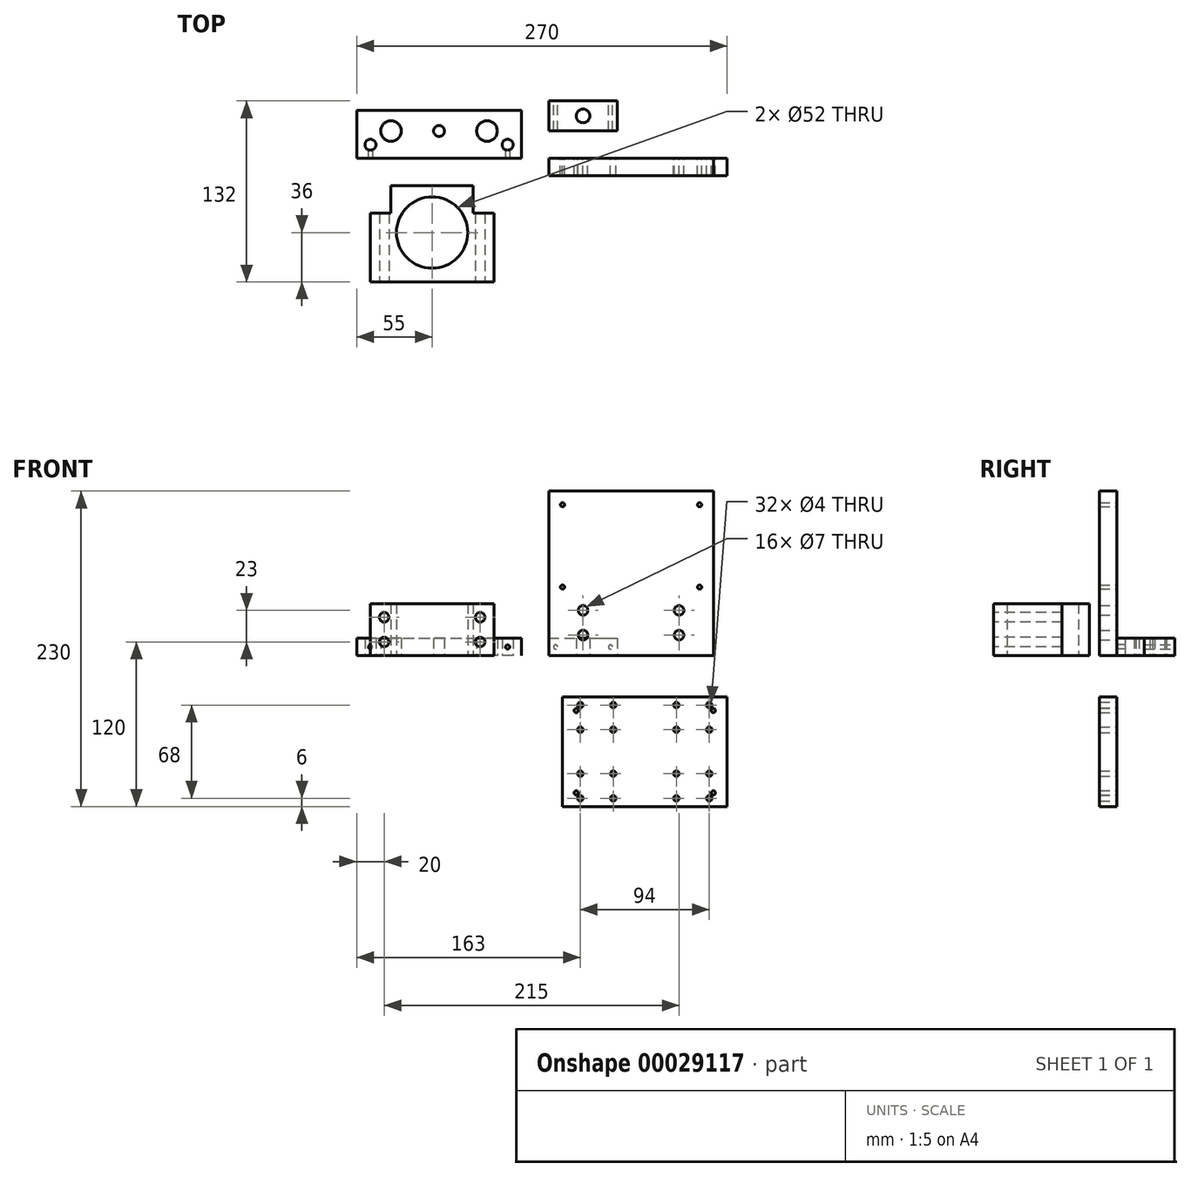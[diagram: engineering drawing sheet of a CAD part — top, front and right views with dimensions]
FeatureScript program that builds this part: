
annotation { "Feature Type Name" : "Feature", "Feature Type Description" : "" }
export const myFeature = defineFeature(function(context is Context, id is Id, definition is map)
    precondition{}
    {
        {
            var Q0;
            Q0=qCreatedBy(makeId("Top.planeOp"),FACE);
            var sketch = newSketch(context, id + "F0", { "sketchPlane" : qUnion([Q0])});
            skLineSegment(sketch, "E0.bottom", {"start": v(-120, 35) * mm, "end": v(0, 35) * mm});
            skLineSegment(sketch, "E0.top", {"start": v(-120, 0) * mm, "end": v(0, 0) * mm});
            skLineSegment(sketch, "E0.left", {"start": v(-120, 35) * mm, "end": v(-120, 0) * mm});
            skLineSegment(sketch, "E0.right", {"start": v(0, 35) * mm, "end": v(0, 0) * mm});
            skCircle(sketch, "E1", {"center": v(-95, 20) * mm, "radius": 7.5 * mm});
            skCircle(sketch, "E2", {"center": v(-60, 20) * mm, "radius": 4 * mm});
            skCircle(sketch, "E3", {"center": v(-25, 20) * mm, "radius": 7.5 * mm});
            skCircle(sketch, "E4", {"center": v(-110, 10) * mm, "radius": 4 * mm});
            skCircle(sketch, "E5", {"center": v(-10, 10) * mm, "radius": 4 * mm});
            skSolve(sketch);
        }
        {
            var Q0;
            Q0 = qSketchRegion(id + "F0", true);
            extrude(context, id + "F1", {"entities" : qUnion([Q0]), "depth" : 12.7 * mm});
        }
        {
            var Q0;
            Q0=makeQuery(id+"F1.opExtrude","SWEPT_FACE",FACE,{"disambiguationData":[OSD([sQuery(id+"F0.wireOp",EDGE,"E0.top")])]});
            var sketch = newSketch(context, id + "F2", { "sketchPlane" : qUnion([Q0])});
            skCircle(sketch, "E6", {"center": v(-110, 6.35) * mm, "radius": 1.5 * mm});
            skCircle(sketch, "E7", {"center": v(-10, 6.35) * mm, "radius": 1.5 * mm});
            skSolve(sketch);
        }
        {
            var Q0;
            Q0 = qSketchRegion(id + "F2", true);
            extrude(context, id + "F3", {"entities" : qUnion([Q0]), "operationType" : NewBodyOperationType.REMOVE, "endBound" : BoundingType.UP_TO_NEXT, "oppositeDirection" : true, "depth" : 25 * mm});
        }
        {
            var Q0;
            Q0=qCreatedBy(makeId("Front.planeOp"),FACE);
            var sketch = newSketch(context, id + "F4", { "sketchPlane" : qUnion([Q0])});
            skLineSegment(sketch, "E8.bottom", {"start": v(20, 120) * mm, "end": v(140, 120) * mm});
            skLineSegment(sketch, "E8.top", {"start": v(20, 0) * mm, "end": v(140, 0) * mm});
            skLineSegment(sketch, "E8.left", {"start": v(20, 120) * mm, "end": v(20, 0) * mm});
            skLineSegment(sketch, "E8.right", {"start": v(140, 120) * mm, "end": v(140, 0) * mm});
            skCircle(sketch, "E9", {"center": v(30, 110) * mm, "radius": 1.5 * mm});
            skCircle(sketch, "E10", {"center": v(130, 110) * mm, "radius": 1.5 * mm});
            skCircle(sketch, "E11", {"center": v(30, 50) * mm, "radius": 1.5 * mm});
            skCircle(sketch, "E12", {"center": v(130, 50) * mm, "radius": 1.5 * mm});
            skCircle(sketch, "E13", {"center": v(45, 33) * mm, "radius": 3.5 * mm});
            skCircle(sketch, "E14", {"center": v(45, 15) * mm, "radius": 3.5 * mm});
            skCircle(sketch, "E15", {"center": v(115, 15) * mm, "radius": 3.5 * mm});
            skCircle(sketch, "E16", {"center": v(115, 33) * mm, "radius": 3.5 * mm});
            skSolve(sketch);
        }
        {
            var Q0;
            Q0 = qSketchRegion(id + "F4", true);
            extrude(context, id + "F5", {"entities" : qUnion([Q0]), "depth" : 12.7 * mm});
        }
        {
            var Q0;
            Q0=qCreatedBy(makeId("Top.planeOp"),FACE);
            var sketch = newSketch(context, id + "F6", { "sketchPlane" : qUnion([Q0])});
            skLineSegment(sketch, "E17", {"start": v(-110, -90) * mm, "end": v(-110, -40) * mm});
            skLineSegment(sketch, "E18", {"start": v(-110, -40) * mm, "end": v(-95, -40) * mm});
            skLineSegment(sketch, "E19", {"start": v(-95, -40) * mm, "end": v(-95, -20) * mm});
            skLineSegment(sketch, "E20", {"start": v(-95, -20) * mm, "end": v(-35, -20) * mm});
            skLineSegment(sketch, "E21", {"start": v(-35, -20) * mm, "end": v(-35, -40) * mm});
            skLineSegment(sketch, "E22", {"start": v(-35, -40) * mm, "end": v(-20, -40) * mm});
            skLineSegment(sketch, "E23", {"start": v(-20, -40) * mm, "end": v(-20, -90) * mm});
            skLineSegment(sketch, "E24", {"start": v(-20, -90) * mm, "end": v(-110, -90) * mm});
            skCircle(sketch, "E25", {"center": v(-65, -54) * mm, "radius": 26 * mm});
            skSolve(sketch);
        }
        {
            var Q0;
            Q0 = qSketchRegion(id + "F6", true);
            extrude(context, id + "F7", {"entities" : qUnion([Q0]), "depth" : 38 * mm});
        }
        {
            var Q0;
            Q0=makeQuery(id+"F7.opExtrude","SWEPT_FACE",FACE,{"disambiguationData":[OSD([sQuery(id+"F6.wireOp",EDGE,"E24")])]});
            var sketch = newSketch(context, id + "F8", { "sketchPlane" : qUnion([Q0])});
            skCircle(sketch, "E26", {"center": v(-100, 28) * mm, "radius": 3.5 * mm});
            skCircle(sketch, "E27", {"center": v(-100, 10) * mm, "radius": 3.5 * mm});
            skCircle(sketch, "E28", {"center": v(-30, 28) * mm, "radius": 3.5 * mm});
            skCircle(sketch, "E29", {"center": v(-30, 10) * mm, "radius": 3.5 * mm});
            skSolve(sketch);
        }
        {
            var Q0;
            Q0 = qSketchRegion(id + "F8", true);
            extrude(context, id + "F9", {"entities" : qUnion([Q0]), "operationType" : NewBodyOperationType.REMOVE, "endBound" : BoundingType.UP_TO_NEXT, "oppositeDirection" : true, "depth" : 25 * mm});
        }
        {
            var Q0;
            Q0=qCreatedBy(makeId("Front.planeOp"),FACE);
            var sketch = newSketch(context, id + "F10", { "sketchPlane" : qUnion([Q0])});
            skLineSegment(sketch, "E30.bottom", {"start": v(150, -30) * mm, "end": v(30, -30) * mm});
            skLineSegment(sketch, "E30.top", {"start": v(150, -110) * mm, "end": v(30, -110) * mm});
            skLineSegment(sketch, "E30.left", {"start": v(150, -30) * mm, "end": v(150, -110) * mm});
            skLineSegment(sketch, "E30.right", {"start": v(30, -30) * mm, "end": v(30, -110) * mm});
            skCircle(sketch, "E31", {"center": v(140, -40) * mm, "radius": 1.5 * mm});
            skCircle(sketch, "E32.0.1.0", {"center": v(140, -100) * mm, "radius": 1.5 * mm});
            skCircle(sketch, "E32.1.0.0", {"center": v(40, -40) * mm, "radius": 1.5 * mm});
            skCircle(sketch, "E32.1.1.0", {"center": v(40, -100) * mm, "radius": 1.5 * mm});
            skLineSegment(sketch, "E32.direction1", {"start": v(140, -40) * mm, "end": v(40, -40) * mm, "construction": true});
            skLineSegment(sketch, "E32.direction2", {"start": v(140, -40) * mm, "end": v(140, -100) * mm, "construction": true});
            skLineSegment(sketch, "E33", {"start": v(140, -100) * mm, "end": v(40, -40) * mm, "construction": true});
            skLineSegment(sketch, "E34", {"start": v(150, -30) * mm, "end": v(30, -110) * mm, "construction": true});
            skPoint(sketch, "E35", {"position": v(90, -70) * mm});
            skPoint(sketch, "E36", {"position": v(55, -45) * mm});
            skPoint(sketch, "E37.0.1.0", {"position": v(55, -95) * mm});
            skPoint(sketch, "E37.1.0.0", {"position": v(125, -45) * mm});
            skPoint(sketch, "E37.1.1.0", {"position": v(125, -95) * mm});
            skLineSegment(sketch, "E37.direction1", {"start": v(55, -45) * mm, "end": v(125, -45) * mm, "construction": true});
            skLineSegment(sketch, "E37.direction2", {"start": v(55, -45) * mm, "end": v(55, -95) * mm, "construction": true});
            skLineSegment(sketch, "E38", {"start": v(125, -95) * mm, "end": v(55, -45) * mm, "construction": true});
            skCircle(sketch, "E39", {"center": v(113, -36) * mm, "radius": 2 * mm});
            skCircle(sketch, "E40.0.1.0", {"center": v(113, -54) * mm, "radius": 2 * mm});
            skCircle(sketch, "E40.1.0.0", {"center": v(137, -36) * mm, "radius": 2 * mm});
            skCircle(sketch, "E40.1.1.0", {"center": v(137, -54) * mm, "radius": 2 * mm});
            skLineSegment(sketch, "E40.direction1", {"start": v(113, -36) * mm, "end": v(137, -36) * mm, "construction": true});
            skLineSegment(sketch, "E40.direction2", {"start": v(113, -36) * mm, "end": v(113, -54) * mm, "construction": true});
            skLineSegment(sketch, "E41", {"start": v(137, -54) * mm, "end": v(113, -36) * mm, "construction": true});
            skCircle(sketch, "E42.0.1.0", {"center": v(43, -54) * mm, "radius": 2 * mm});
            skCircle(sketch, "E42.1.1.0", {"center": v(67, -54) * mm, "radius": 2 * mm});
            skCircle(sketch, "E43", {"center": v(43, -36) * mm, "radius": 2 * mm});
            skLineSegment(sketch, "E42.direction2", {"start": v(43, -36) * mm, "end": v(43, -54) * mm, "construction": true});
            skLineSegment(sketch, "E44", {"start": v(67, -54) * mm, "end": v(43, -36) * mm, "construction": true});
            skCircle(sketch, "E42.1.0.0", {"center": v(67, -36) * mm, "radius": 2 * mm});
            skLineSegment(sketch, "E42.direction1", {"start": v(43, -36) * mm, "end": v(67, -36) * mm, "construction": true});
            skCircle(sketch, "E45.0.1.0", {"center": v(113, -104) * mm, "radius": 2 * mm});
            skCircle(sketch, "E45.1.1.0", {"center": v(137, -104) * mm, "radius": 2 * mm});
            skCircle(sketch, "E46", {"center": v(113, -86) * mm, "radius": 2 * mm});
            skLineSegment(sketch, "E45.direction2", {"start": v(113, -86) * mm, "end": v(113, -104) * mm, "construction": true});
            skLineSegment(sketch, "E47", {"start": v(137, -104) * mm, "end": v(113, -86) * mm, "construction": true});
            skCircle(sketch, "E45.1.0.0", {"center": v(137, -86) * mm, "radius": 2 * mm});
            skLineSegment(sketch, "E45.direction1", {"start": v(113, -86) * mm, "end": v(137, -86) * mm, "construction": true});
            skCircle(sketch, "E48.0.1.0", {"center": v(43, -104) * mm, "radius": 2 * mm});
            skCircle(sketch, "E48.1.1.0", {"center": v(67, -104) * mm, "radius": 2 * mm});
            skCircle(sketch, "E49", {"center": v(43, -86) * mm, "radius": 2 * mm});
            skLineSegment(sketch, "E48.direction2", {"start": v(43, -86) * mm, "end": v(43, -104) * mm, "construction": true});
            skLineSegment(sketch, "E50", {"start": v(67, -104) * mm, "end": v(43, -86) * mm, "construction": true});
            skCircle(sketch, "E48.1.0.0", {"center": v(67, -86) * mm, "radius": 2 * mm});
            skLineSegment(sketch, "E48.direction1", {"start": v(43, -86) * mm, "end": v(67, -86) * mm, "construction": true});
            skSolve(sketch);
        }
        {
            var Q0;
            Q0=makeQuery(id+"F10.imprint","IMPRINT",FACE,{"disambiguationData":[TD([[makeQuery(id+"F10.imprint","IMPRINT",EDGE,{"derivedFrom":sQuery(id+"F10.wireOp",EDGE,"E30.bottom")}),1.0]])]});
            extrude(context, id + "F11", {"entities" : qUnion([Q0]), "depth" : 12.7 * mm});
        }
        {
            var Q0;
            Q0=qCreatedBy(makeId("Top.planeOp"),FACE);
            var sketch = newSketch(context, id + "F12", { "sketchPlane" : qUnion([Q0])});
            skLineSegment(sketch, "E51.bottom", {"start": v(20, 42) * mm, "end": v(70, 42) * mm});
            skLineSegment(sketch, "E51.top", {"start": v(20, 20) * mm, "end": v(70, 20) * mm});
            skLineSegment(sketch, "E51.left", {"start": v(20, 42) * mm, "end": v(20, 20) * mm});
            skLineSegment(sketch, "E51.right", {"start": v(70, 42) * mm, "end": v(70, 20) * mm});
            skLineSegment(sketch, "E52", {"start": v(45, 42) * mm, "end": v(45, 20) * mm, "construction": true});
            skCircle(sketch, "E53", {"center": v(45, 31) * mm, "radius": 5 * mm});
            skSolve(sketch);
        }
        {
            var Q0;
            Q0 = qSketchRegion(id + "F12", true);
            extrude(context, id + "F13", {"entities" : qUnion([Q0]), "depth" : 12.7 * mm});
        }
        {
            var Q0;
            Q0=makeQuery(id+"F13.opExtrude","SWEPT_FACE",FACE,{"disambiguationData":[OSD([sQuery(id+"F12.wireOp",EDGE,"E51.bottom")])]});
            var sketch = newSketch(context, id + "F14", { "sketchPlane" : qUnion([Q0])});
            skCircle(sketch, "E54", {"center": v(-65, 6.35) * mm, "radius": 1.5 * mm});
            skCircle(sketch, "E55", {"center": v(-25, 6.35) * mm, "radius": 1.5 * mm});
            skLineSegment(sketch, "E56", {"start": v(-65, 6.35) * mm, "end": v(-25, 6.35) * mm, "construction": true});
            skLineSegment(sketch, "E57", {"start": v(-70, 12.7) * mm, "end": v(-20, 0) * mm, "construction": true});
            skPoint(sketch, "E58", {"position": v(-45, 6.35) * mm});
            skSolve(sketch);
        }
        {
            var Q0;
            Q0 = qSketchRegion(id + "F14", true);
            extrude(context, id + "F15", {"entities" : qUnion([Q0]), "operationType" : NewBodyOperationType.REMOVE, "endBound" : BoundingType.UP_TO_NEXT, "oppositeDirection" : true, "depth" : 25 * mm});
        }
    });
